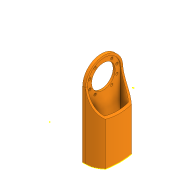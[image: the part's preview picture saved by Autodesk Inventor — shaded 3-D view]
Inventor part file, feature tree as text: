
AUTODESK INVENTOR PART (.ipt)
format: ipt  version: 2020 (Build 240168000, 168)  size: 227,328 bytes
history: native  units: in
note: dims shown in document units (in); Inventor stores cm internally (conversion verified against a paired STEP export)
features: sketch x7, extrude x4, projected_geometry x2
ambient origin geometry x8: Origin, YZ Plane, XZ Plane, XY Plane, X Axis, Y Axis, Z Axis, Center Point
bodies: Solid1 (feature_tree)
feature tree (13):
  extrude  "Extrusion1"  Depth=0.2362in
  sketch  "Sketch2"  dims[d6=0.2362in d7=0.2362in]
  extrude  "Extrusion2"  Depth=0.2362in
  sketch  "Sketch4"  dims[d10=0.2362in d11=0.2362in]
  extrude  "Extrusion3"  Depth=0.2362in
  extrude  "Extrusion4"  Depth=0.2362in
  sketch  "Sketch7"  dims[d14=0.1969in d15=0.0in d16=0.0394in d17=0.0394in d18=0.1969in d19=0.1969in d20=0.0787in d21=0.0in d22=1.7717in d23=1.2598in d24=2.5197in d25=0.1181in d26=0.1969in d27=6.4173in d28=0.0in d29=1.1811in d30=6.4173in d31=0.0in]
  sketch  "Sketch1"  dims[d3=2.3622in d5=0.2362in]
  sketch  "Sketch3"  dims[d8=0.2362in d9=0.2362in]
  sketch  "Sketch5"  dims[d12=0.2362in]
  sketch  "Sketch6"  dims[d13=4.85in]
  projected_geometry  "Projected Loop1"
  projected_geometry  "Projected Loop2"
